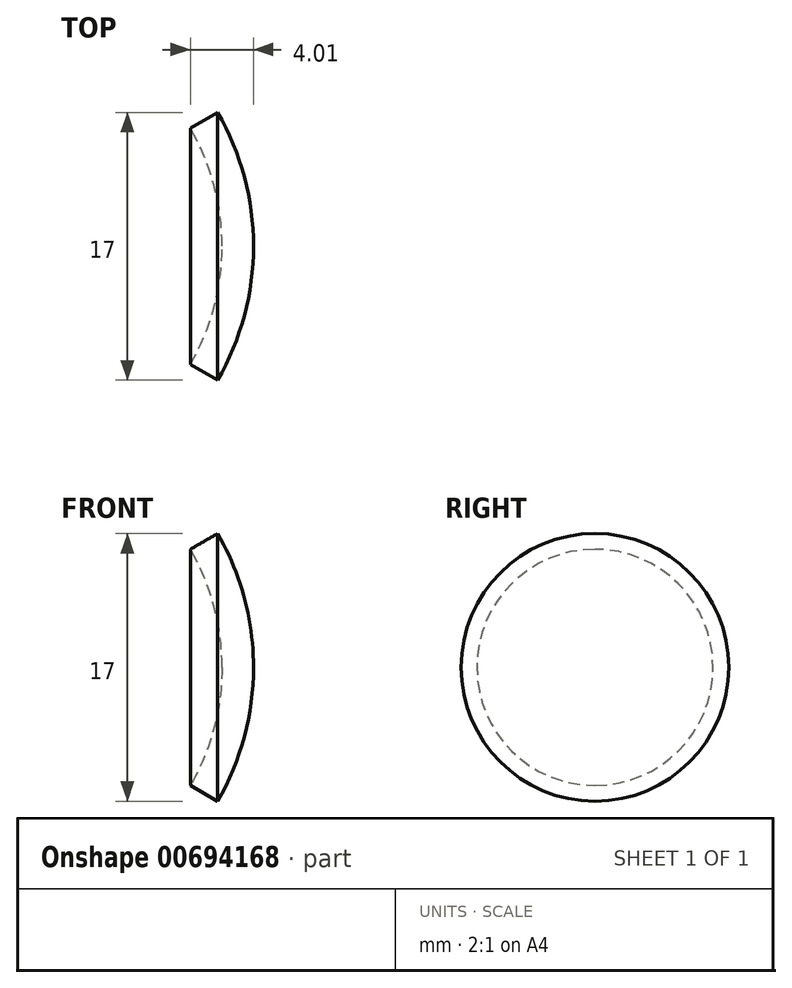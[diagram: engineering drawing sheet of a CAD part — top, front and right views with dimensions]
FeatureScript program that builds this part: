
annotation { "Feature Type Name" : "Feature", "Feature Type Description" : "" }
export const myFeature = defineFeature(function(context is Context, id is Id, definition is map)
    precondition{}
    {
        {
            var Q0;
            Q0=qCreatedBy(makeId("Front.planeOp"),FACE);
            var sketch = newSketch(context, id + "F0", { "sketchPlane" : qUnion([Q0])});
            skLineSegment(sketch, "E0", {"start": v(15, 0) * mm, "end": v(17, 0) * mm});
            skArc(sketch, "E1", {"start": v(17, 0) * mm, "mid": v(16.42, 4.4) * mm, "end": v(14.72, 8.5) * mm});
            skArc(sketch, "E2", {"start": v(15, 0) * mm, "mid": v(14.49, 3.88) * mm, "end": v(13, 7.5) * mm});
            skLineSegment(sketch, "E3", {"start": v(14.72, 8.5) * mm, "end": v(13, 7.5) * mm});
            skSolve(sketch);
        }
        {
            var Q0;
            Q0=makeQuery(id+"F0.imprint","IMPRINT",FACE,{"disambiguationData":[TD([[makeQuery(id+"F0.imprint","IMPRINT",EDGE,{"derivedFrom":sQuery(id+"F0.wireOp",EDGE,"E0")}),1.0]])]});
            var Q1;
            Q1=sQuery(id+"F0.wireOp",EDGE,"E0");
            revolve(context, id + "F1", {"entities" : qUnion([Q0]), "axis" : qUnion([Q1]), "revolveType" : RevolveType.FULL});
        }
    });
